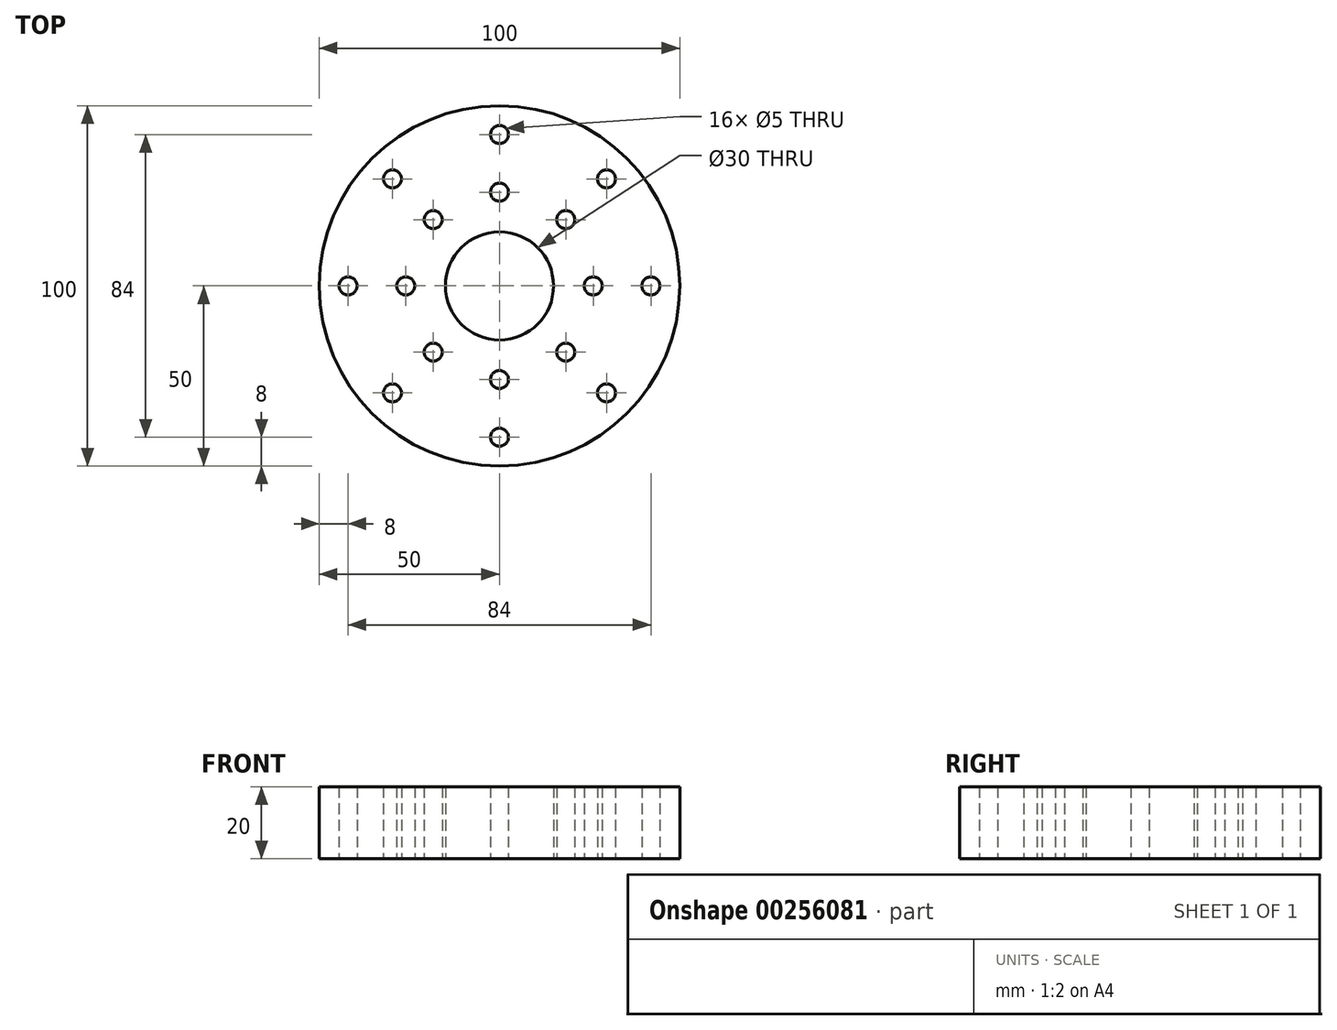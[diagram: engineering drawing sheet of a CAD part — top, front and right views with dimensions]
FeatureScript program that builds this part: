
annotation { "Feature Type Name" : "Feature", "Feature Type Description" : "" }
export const myFeature = defineFeature(function(context is Context, id is Id, definition is map)
    precondition{}
    {
        {
            var Q0;
            Q0=qCreatedBy(makeId("Top.planeOp"),FACE);
            var sketch = newSketch(context, id + "F0", { "sketchPlane" : qUnion([Q0])});
            skCircle(sketch, "E0", {"center": v(0, 0) * mm, "radius": 15 * mm});
            skCircle(sketch, "E1", {"center": v(0, 0) * mm, "radius": 50 * mm});
            skLineSegment(sketch, "E2", {"start": v(0, 0) * mm, "end": v(50, 0) * mm, "construction": true});
            skCircle(sketch, "E3", {"center": v(42, 0) * mm, "radius": 2.5 * mm});
            skCircle(sketch, "E4", {"center": v(26, 0) * mm, "radius": 2.5 * mm});
            skCircle(sketch, "E5.1.0", {"center": v(18.38, 18.38) * mm, "radius": 2.5 * mm});
            skCircle(sketch, "E5.1.1", {"center": v(29.7, 29.7) * mm, "radius": 2.5 * mm});
            skCircle(sketch, "E5.2.0", {"center": v(0, 26) * mm, "radius": 2.5 * mm});
            skCircle(sketch, "E5.2.1", {"center": v(0, 42) * mm, "radius": 2.5 * mm});
            skCircle(sketch, "E5.3.0", {"center": v(-18.38, 18.38) * mm, "radius": 2.5 * mm});
            skCircle(sketch, "E5.3.1", {"center": v(-29.7, 29.7) * mm, "radius": 2.5 * mm});
            skCircle(sketch, "E5.4.0", {"center": v(-26, 0) * mm, "radius": 2.5 * mm});
            skCircle(sketch, "E5.4.1", {"center": v(-42, 0) * mm, "radius": 2.5 * mm});
            skCircle(sketch, "E5.5.0", {"center": v(-18.38, -18.38) * mm, "radius": 2.5 * mm});
            skCircle(sketch, "E5.5.1", {"center": v(-29.7, -29.7) * mm, "radius": 2.5 * mm});
            skCircle(sketch, "E5.6.0", {"center": v(0, -26) * mm, "radius": 2.5 * mm});
            skCircle(sketch, "E5.6.1", {"center": v(0, -42) * mm, "radius": 2.5 * mm});
            skCircle(sketch, "E5.7.0", {"center": v(18.38, -18.38) * mm, "radius": 2.5 * mm});
            skCircle(sketch, "E5.7.1", {"center": v(29.7, -29.7) * mm, "radius": 2.5 * mm});
            skSolve(sketch);
        }
        {
            var Q0;
            Q0 = qSketchRegion(id + "F0", true);
            extrude(context, id + "F1", {"entities" : qUnion([Q0]), "depth" : 20 * mm});
        }
    });
